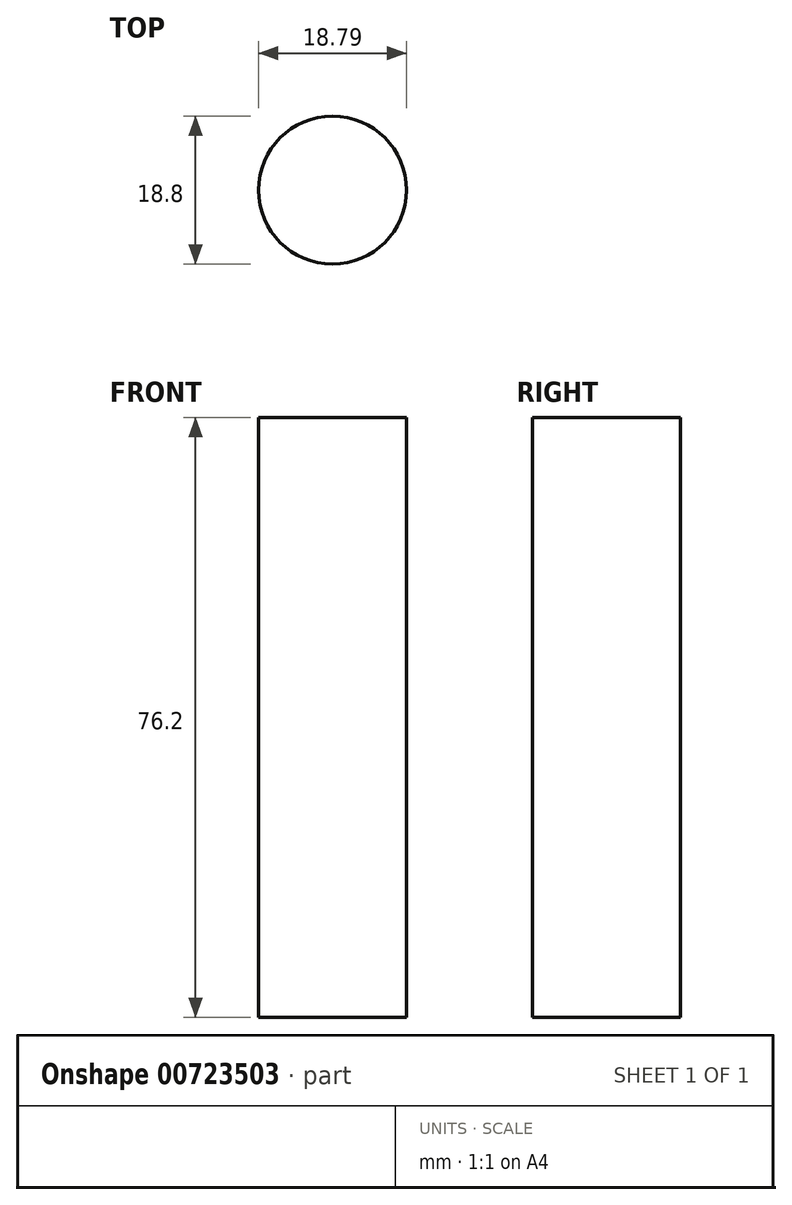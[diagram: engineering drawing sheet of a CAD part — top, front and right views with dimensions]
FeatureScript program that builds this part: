
annotation { "Feature Type Name" : "Feature", "Feature Type Description" : "" }
export const myFeature = defineFeature(function(context is Context, id is Id, definition is map)
    precondition{}
    {
        {
            var Q0;
            Q0=qCreatedBy(makeId("Top.planeOp"),FACE);
            var sketch = newSketch(context, id + "F0", { "sketchPlane" : qUnion([Q0])});
            skCircle(sketch, "E0", {"center": v(-69.69, -47.98) * mm, "radius": 9.4 * mm});
            skSolve(sketch);
        }
        {
            var Q0;
            Q0=makeQuery(id+"F0.imprint","IMPRINT",FACE,{"disambiguationData":[TD([[makeQuery(id+"F0.imprint","IMPRINT",EDGE,{"derivedFrom":sQuery(id+"F0.wireOp",EDGE,"E0")}),1.0]])]});
            extrude(context, id + "F1", {"entities" : qUnion([Q0]), "depth" : 76.2 * mm, "offsetDistance" : 25.4 * mm});
        }
    });
